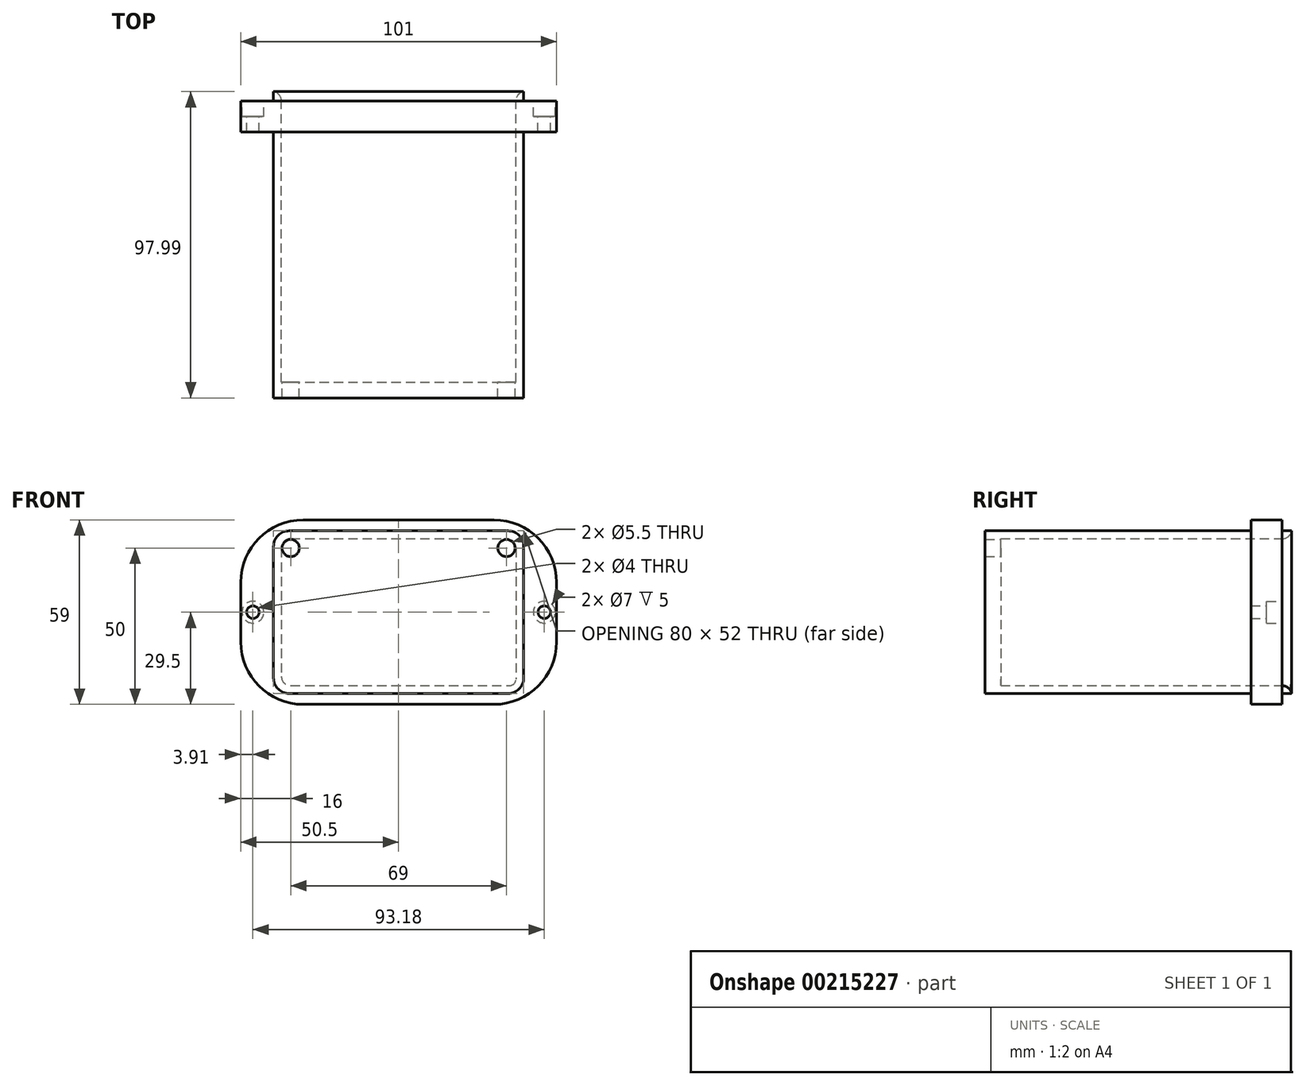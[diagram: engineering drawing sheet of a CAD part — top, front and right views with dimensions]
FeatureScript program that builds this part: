
annotation { "Feature Type Name" : "Feature", "Feature Type Description" : "" }
export const myFeature = defineFeature(function(context is Context, id is Id, definition is map)
    precondition{}
    {
        {
            var Q0;
            Q0=qCreatedBy(makeId("Front.planeOp"),FACE);
            var sketch = newSketch(context, id + "F0", { "sketchPlane" : qUnion([Q0])});
            skLineSegment(sketch, "E0.bottom", {"start": v(-30.5, 29.5) * mm, "end": v(30.5, 29.5) * mm});
            skLineSegment(sketch, "E0.top", {"start": v(-30.5, -29.5) * mm, "end": v(30.5, -29.5) * mm});
            skLineSegment(sketch, "E0.left", {"start": v(-50.5, 9.5) * mm, "end": v(-50.5, -9.5) * mm});
            skLineSegment(sketch, "E0.right", {"start": v(50.5, 9.5) * mm, "end": v(50.5, -9.5) * mm});
            skPoint(sketch, "E0.middle", {"position": v(0, 0) * mm});
            skLineSegment(sketch, "E1.bottom", {"start": v(-34.5, 23.5) * mm, "end": v(34.5, 23.5) * mm});
            skLineSegment(sketch, "E1.top", {"start": v(-34.5, -23.5) * mm, "end": v(35.5, -23.5) * mm});
            skLineSegment(sketch, "E1.left", {"start": v(-37.5, 20.5) * mm, "end": v(-37.5, -20.5) * mm});
            skLineSegment(sketch, "E1.right", {"start": v(37.5, 20.5) * mm, "end": v(37.5, -21.5) * mm});
            skPoint(sketch, "E2.visualSharp", {"position": v(-50.5, 29.5) * mm});
            skArc(sketch, "E2.filletArc", {"start": v(-30.5, 29.5) * mm, "mid": v(-44.64, 23.64) * mm, "end": v(-50.5, 9.5) * mm});
            skPoint(sketch, "E3.visualSharp", {"position": v(-50.5, -29.5) * mm});
            skArc(sketch, "E3.filletArc", {"start": v(-50.5, -9.5) * mm, "mid": v(-44.64, -23.64) * mm, "end": v(-30.5, -29.5) * mm});
            skPoint(sketch, "E4.visualSharp", {"position": v(50.5, 29.5) * mm});
            skArc(sketch, "E4.filletArc", {"start": v(50.5, 9.5) * mm, "mid": v(44.64, 23.64) * mm, "end": v(30.5, 29.5) * mm});
            skPoint(sketch, "E5.visualSharp", {"position": v(50.5, -29.5) * mm});
            skArc(sketch, "E5.filletArc", {"start": v(30.5, -29.5) * mm, "mid": v(44.64, -23.64) * mm, "end": v(50.5, -9.5) * mm});
            skPoint(sketch, "E6.visualSharp", {"position": v(40, -26) * mm});
            skPoint(sketch, "E7.visualSharp", {"position": v(37.5, -23.5) * mm});
            skArc(sketch, "E7.filletArc", {"start": v(35.5, -23.5) * mm, "mid": v(36.91, -22.91) * mm, "end": v(37.5, -21.5) * mm});
            skPoint(sketch, "E8.visualSharp", {"position": v(39.47, 25.63) * mm});
            skPoint(sketch, "E9.visualSharp", {"position": v(-40, 26) * mm});
            skPoint(sketch, "E10.visualSharp", {"position": v(-39.47, -25.63) * mm});
            skPoint(sketch, "E11.visualSharp", {"position": v(37.5, 23.5) * mm});
            skArc(sketch, "E11.filletArc", {"start": v(37.5, 20.5) * mm, "mid": v(36.62, 22.62) * mm, "end": v(34.5, 23.5) * mm});
            skPoint(sketch, "E12.visualSharp", {"position": v(-37.5, 23.5) * mm});
            skArc(sketch, "E12.filletArc", {"start": v(-34.5, 23.5) * mm, "mid": v(-36.62, 22.62) * mm, "end": v(-37.5, 20.5) * mm});
            skPoint(sketch, "E13.visualSharp", {"position": v(-37.5, -23.5) * mm});
            skArc(sketch, "E13.filletArc", {"start": v(-37.5, -20.5) * mm, "mid": v(-36.62, -22.62) * mm, "end": v(-34.5, -23.5) * mm});
            skCircle(sketch, "E14", {"center": v(46.6, 0) * mm, "radius": 2 * mm});
            skCircle(sketch, "E15", {"center": v(-46.6, 0) * mm, "radius": 2 * mm});
            skPoint(sketch, "E16", {"position": v(-39.7, 20.28) * mm});
            skPoint(sketch, "E17", {"position": v(39.5, 20.63) * mm});
            skPoint(sketch, "E18", {"position": v(-34.78, -20.72) * mm});
            skPoint(sketch, "E19", {"position": v(-6.77, -20.72) * mm});
            skPoint(sketch, "E20", {"position": v(-37.5, 0) * mm});
            skPoint(sketch, "E21", {"position": v(37.5, -0.5) * mm});
            skPoint(sketch, "E22", {"position": v(-42.4, 0) * mm});
            skPoint(sketch, "E23", {"position": v(39.6, 0) * mm});
            skLineSegment(sketch, "E24.bottom", {"start": v(-35, 26) * mm, "end": v(35, 26) * mm});
            skLineSegment(sketch, "E24.top", {"start": v(-35, -26) * mm, "end": v(35, -26) * mm});
            skLineSegment(sketch, "E24.left", {"start": v(-40, 21) * mm, "end": v(-40, -21) * mm});
            skLineSegment(sketch, "E24.right", {"start": v(40, 21) * mm, "end": v(40, -21) * mm});
            skPoint(sketch, "E25.visualSharp", {"position": v(40, 26) * mm});
            skArc(sketch, "E25.filletArc", {"start": v(40, 21) * mm, "mid": v(38.54, 24.54) * mm, "end": v(35, 26) * mm});
            skArc(sketch, "E26.filletArc", {"start": v(35, -26) * mm, "mid": v(38.54, -24.54) * mm, "end": v(40, -21) * mm});
            skPoint(sketch, "E27.visualSharp", {"position": v(-40, -26) * mm});
            skArc(sketch, "E27.filletArc", {"start": v(-40, -21) * mm, "mid": v(-38.54, -24.54) * mm, "end": v(-35, -26) * mm});
            skArc(sketch, "E28.filletArc", {"start": v(-35, 26) * mm, "mid": v(-38.54, 24.54) * mm, "end": v(-40, 21) * mm});
            skCircle(sketch, "E29", {"center": v(-46.6, 0) * mm, "radius": 3.5 * mm});
            skCircle(sketch, "E30", {"center": v(46.6, 0) * mm, "radius": 3.5 * mm});
            skPoint(sketch, "E31", {"position": v(-37.5, 20.5) * mm});
            skPoint(sketch, "E32", {"position": v(-34.5, 23.5) * mm});
            skPoint(sketch, "E33", {"position": v(-34.5, 18.56) * mm});
            skPoint(sketch, "E34", {"position": v(-32.93, 20.5) * mm});
            skLineSegment(sketch, "E35", {"start": v(-37.5, 20.5) * mm, "end": v(-32.93, 20.5) * mm, "construction": true});
            skLineSegment(sketch, "E36", {"start": v(-34.5, 18.56) * mm, "end": v(-34.5, 23.5) * mm, "construction": true});
            skPoint(sketch, "E37", {"position": v(37.5, 20.5) * mm});
            skPoint(sketch, "E38", {"position": v(34.5, 23.5) * mm});
            skLineSegment(sketch, "E39", {"start": v(34.5, 23.5) * mm, "end": v(34.5, 19.26) * mm, "construction": true});
            skLineSegment(sketch, "E40", {"start": v(37.5, 20.5) * mm, "end": v(31.87, 20.5) * mm, "construction": true});
            skCircle(sketch, "E41", {"center": v(-34.5, 20.5) * mm, "radius": 2.75 * mm});
            skCircle(sketch, "E42", {"center": v(34.5, 20.5) * mm, "radius": 2.75 * mm});
            skSolve(sketch);
        }
        {
            var Q0;
            Q0=makeQuery(id+"F0.imprint","IMPRINT",FACE,{"disambiguationData":[TD([[makeQuery(id+"F0.imprint","IMPRINT",EDGE,{"derivedFrom":sQuery(id+"F0.wireOp",EDGE,"E0.bottom")}),-1.0]])]});
            extrude(context, id + "F1", {"entities" : qUnion([Q0]), "depth" : 10 * mm});
        }
        {
            var Q0;
            Q0=makeQuery(id+"F0.imprint","IMPRINT",FACE,{"disambiguationData":[TD([[makeQuery(id+"F0.imprint","IMPRINT",EDGE,{"derivedFrom":sQuery(id+"F0.wireOp",EDGE,"E1.bottom")}),1.0]])]});
            var Q1;
            Q1=makeQuery(id+"F0.imprint","IMPRINT",FACE,{"disambiguationData":[TD([[makeQuery(id+"F0.imprint","IMPRINT",EDGE,{"derivedFrom":sQuery(id+"F0.wireOp",EDGE,"E1.bottom")}),-1.0]])]});
            extrude(context, id + "F2", {"entities" : qUnion([Q0, Q1]), "operationType" : NewBodyOperationType.ADD, "depth" : 95 * mm});
        }
        {
            var Q0;
            Q0=makeQuery(id+"F0.imprint","IMPRINT",FACE,{"disambiguationData":[TD([[makeQuery(id+"F0.imprint","IMPRINT",EDGE,{"derivedFrom":sQuery(id+"F0.wireOp",EDGE,"E1.bottom")}),-1.0]])]});
            extrude(context, id + "F3", {"entities" : qUnion([Q0]), "operationType" : NewBodyOperationType.REMOVE, "depth" : 90 * mm});
        }
        {
            var Q0;
            Q0=makeQuery(id+"F0.imprint","IMPRINT",FACE,{"disambiguationData":[TD([[makeQuery(id+"F0.imprint","IMPRINT",EDGE,{"derivedFrom":sQuery(id+"F0.wireOp",EDGE,"E1.bottom")}),1.0]])]});
            extrude(context, id + "F4", {"entities" : qUnion([Q0]), "operationType" : NewBodyOperationType.ADD, "oppositeDirection" : true, "depth" : 3 * mm});
        }
        {
            var Q0;
            Q0=makeQuery(id+"F4.opExtrude","CAP_EDGE",EDGE,{"disambiguationData":[OSD([sQuery(id+"F0.wireOp",EDGE,"E1.left")])],"isStart":false});
            var Q1;
            Q1=makeQuery(id+"F4.opExtrude","CAP_EDGE",EDGE,{"disambiguationData":[OSD([sQuery(id+"F0.wireOp",EDGE,"E1.top")])],"isStart":false});
            fillet(context, id + "F5", {"entities" : qUnion([Q0, Q1]), "radius" : 3 * mm, "tangentPropagation" : true, "allowEdgeOverflow" : false});
        }
        {
            var Q0;
            Q0=makeQuery(id+"F0.imprint","IMPRINT",FACE,{"disambiguationData":[TD([[makeQuery(id+"F0.imprint","IMPRINT",EDGE,{"derivedFrom":sQuery(id+"F0.wireOp",EDGE,"E14")}),-1.0]])]});
            var Q1;
            Q1=makeQuery(id+"F0.imprint","IMPRINT",FACE,{"disambiguationData":[TD([[makeQuery(id+"F0.imprint","IMPRINT",EDGE,{"derivedFrom":sQuery(id+"F0.wireOp",EDGE,"E15")}),-1.0]])]});
            extrude(context, id + "F6", {"entities" : qUnion([Q0, Q1]), "operationType" : NewBodyOperationType.ADD, "depth" : 10 * mm});
        }
        {
            var Q0;
            Q0=makeQuery(id+"F0.imprint","IMPRINT",FACE,{"disambiguationData":[TD([[makeQuery(id+"F0.imprint","IMPRINT",EDGE,{"derivedFrom":sQuery(id+"F0.wireOp",EDGE,"E14")}),-1.0]])]});
            var Q1;
            Q1=makeQuery(id+"F0.imprint","IMPRINT",FACE,{"disambiguationData":[TD([[makeQuery(id+"F0.imprint","IMPRINT",EDGE,{"derivedFrom":sQuery(id+"F0.wireOp",EDGE,"E15")}),-1.0]])]});
            extrude(context, id + "F7", {"entities" : qUnion([Q0, Q1]), "operationType" : NewBodyOperationType.REMOVE, "depth" : 5 * mm});
        }
    });
